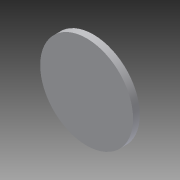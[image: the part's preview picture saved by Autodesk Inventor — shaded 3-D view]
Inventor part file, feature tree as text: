
AUTODESK INVENTOR PART (.ipt)
format: ipt  version: 2014 (Build 180170000, 170)  size: 69,120 bytes
history: native  units: in
note: dims shown in document units (in); Inventor stores cm internally (conversion verified against a paired STEP export)
features: extrude x1, sketch x1
ambient origin geometry x8: Origin, YZ Plane, XZ Plane, XY Plane, X Axis, Y Axis, Z Axis, Center Point
bodies: Solid1 (feature_tree)
feature tree (2):
  extrude  "Extrusion1"  Depth=0.0689in TaperAngle=0.0deg
  sketch  "Sketch1"  dims[d0=0.9551in d1=0.0689in d2=0.0in]
